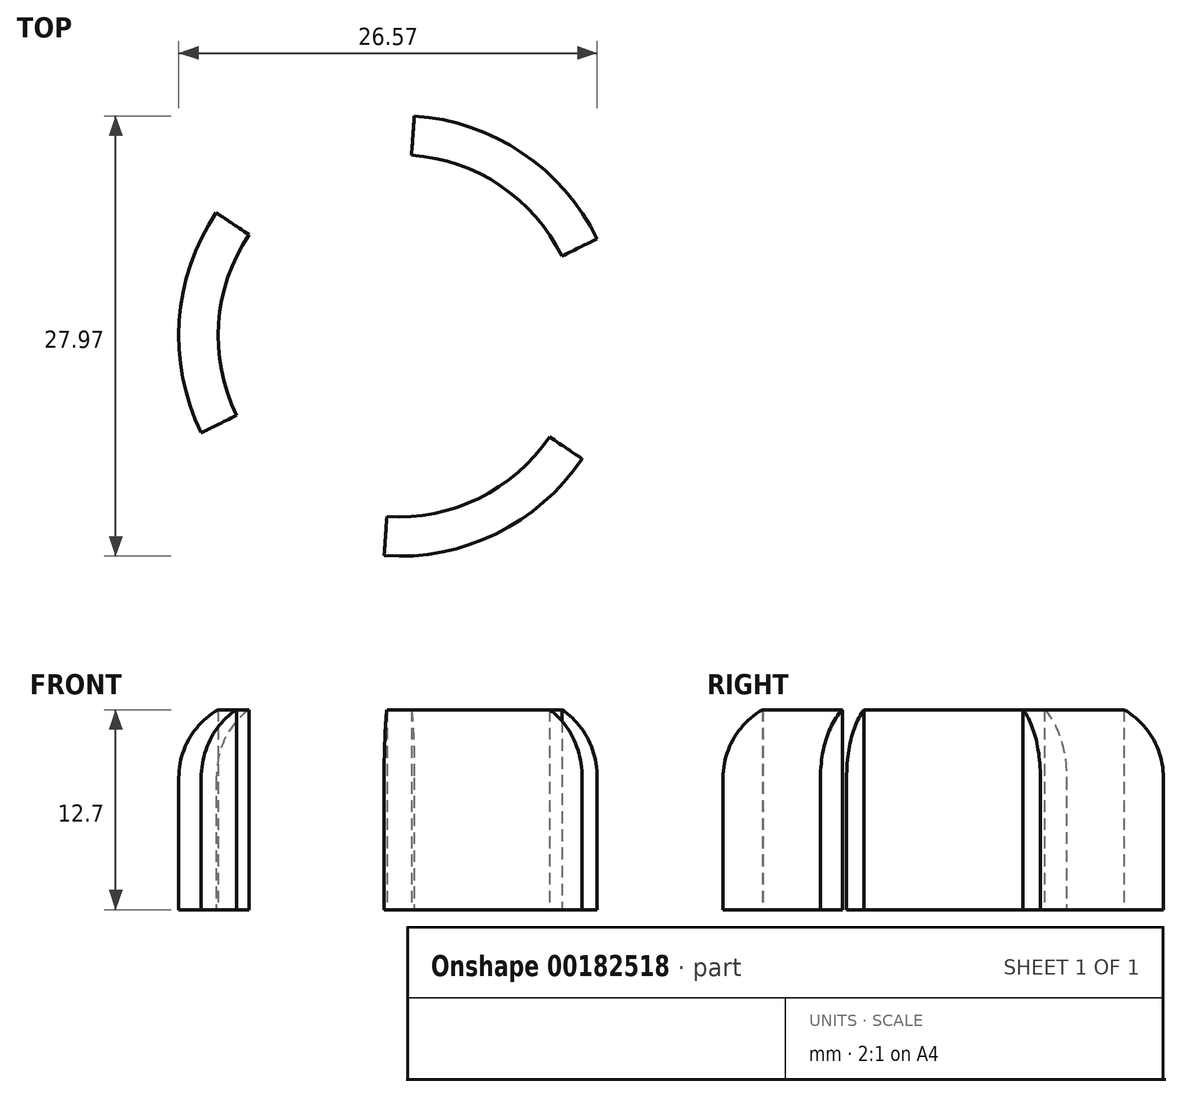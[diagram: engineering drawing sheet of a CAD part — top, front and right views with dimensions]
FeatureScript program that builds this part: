
annotation { "Feature Type Name" : "Feature", "Feature Type Description" : "" }
export const myFeature = defineFeature(function(context is Context, id is Id, definition is map)
    precondition{}
    {
        {
            var Q0;
            Q0=qCreatedBy(makeId("Top.planeOp"),FACE);
            var sketch = newSketch(context, id + "F0", { "sketchPlane" : qUnion([Q0])});
            skCircle(sketch, "E0", {"center": v(0, 0) * mm, "radius": 14 * mm});
            skLineSegment(sketch, "E1", {"start": v(0, 0) * mm, "end": v(12.57, 6.16) * mm});
            skLineSegment(sketch, "E2", {"start": v(0, 0) * mm, "end": v(11.62, -7.81) * mm});
            skLineSegment(sketch, "E3", {"start": v(0, 0) * mm, "end": v(-12.57, -6.16) * mm});
            skLineSegment(sketch, "E4", {"start": v(0, 0) * mm, "end": v(-11.62, 7.81) * mm});
            skLineSegment(sketch, "E5", {"start": v(0, 0) * mm, "end": v(0.96, 13.97) * mm});
            skLineSegment(sketch, "E6", {"start": v(0, 0) * mm, "end": v(-0.96, -13.97) * mm});
            skCircle(sketch, "E7", {"center": v(0, 0) * mm, "radius": 11.5 * mm});
            skSolve(sketch);
        }
        {
            var Q0;
            {var subQ0=sQuery(id+"F0.wireOp",EDGE,"E1");var subQ1=sQuery(id+"F0.wireOp",EDGE,"E0");var subQ2=makeQuery(id+"F0.imprint","INTERSECT",VERTEX,{"derivedFrom":[subQ1,subQ0]});Q0=makeQuery(id+"F0.imprint","IMPRINT",FACE,{"disambiguationData":[TD([[makeQuery(id+"F0.imprint","IMPRINT",EDGE,{"disambiguationData":[TD([[subQ2,-1.0]])],"derivedFrom":subQ1}),1.0]])]});}
            var Q1;
            {var subQ0=sQuery(id+"F0.wireOp",EDGE,"E2");var subQ1=sQuery(id+"F0.wireOp",EDGE,"E0");var subQ2=makeQuery(id+"F0.imprint","INTERSECT",VERTEX,{"derivedFrom":[subQ1,subQ0]});Q1=makeQuery(id+"F0.imprint","IMPRINT",FACE,{"disambiguationData":[TD([[makeQuery(id+"F0.imprint","IMPRINT",EDGE,{"disambiguationData":[TD([[subQ2,1.0]])],"derivedFrom":subQ1}),1.0]])]});}
            var Q2;
            {var subQ0=sQuery(id+"F0.wireOp",EDGE,"E3");var subQ1=sQuery(id+"F0.wireOp",EDGE,"E0");var subQ2=makeQuery(id+"F0.imprint","INTERSECT",VERTEX,{"derivedFrom":[subQ1,subQ0]});Q2=makeQuery(id+"F0.imprint","IMPRINT",FACE,{"disambiguationData":[TD([[makeQuery(id+"F0.imprint","IMPRINT",EDGE,{"disambiguationData":[TD([[subQ2,1.0]])],"derivedFrom":subQ1}),1.0]])]});}
            extrude(context, id + "F1", {"entities" : qUnion([Q0, Q1, Q2]), "depth" : 12.7 * mm});
        }
        {
            var Q0;
            {var subQ0=sQuery(id+"F0.wireOp",EDGE,"E0");Q0=makeQuery(id+"F1.opExtrude","CAP_EDGE",EDGE,{"disambiguationData":[OSD([subQ0]),TDD([makeQuery(id+"F0.imprint","IMPRINT",EDGE,{"disambiguationData":[TD([[makeQuery(id+"F0.imprint","INTERSECT",VERTEX,{"derivedFrom":[subQ0,sQuery(id+"F0.wireOp",EDGE,"E3")]}),1.0]])],"derivedFrom":subQ0})])],"isStart":false});}
            fillet(context, id + "F2", {"entities" : qUnion([Q0]), "radius" : 5 * mm, "tangentPropagation" : true, "allowEdgeOverflow" : false});
        }
        {
            var Q0;
            {var subQ0=sQuery(id+"F0.wireOp",EDGE,"E0");Q0=makeQuery(id+"F1.opExtrude","CAP_EDGE",EDGE,{"disambiguationData":[OSD([subQ0]),TDD([makeQuery(id+"F0.imprint","IMPRINT",EDGE,{"disambiguationData":[TD([[makeQuery(id+"F0.imprint","INTERSECT",VERTEX,{"derivedFrom":[subQ0,sQuery(id+"F0.wireOp",EDGE,"E1")]}),-1.0]])],"derivedFrom":subQ0})])],"isStart":false});}
            fillet(context, id + "F3", {"entities" : qUnion([Q0]), "radius" : 5 * mm, "tangentPropagation" : true, "allowEdgeOverflow" : false});
        }
        {
            var Q0;
            {var subQ0=sQuery(id+"F0.wireOp",EDGE,"E0");Q0=makeQuery(id+"F1.opExtrude","CAP_EDGE",EDGE,{"disambiguationData":[OSD([subQ0]),TDD([makeQuery(id+"F0.imprint","IMPRINT",EDGE,{"disambiguationData":[TD([[makeQuery(id+"F0.imprint","INTERSECT",VERTEX,{"derivedFrom":[subQ0,sQuery(id+"F0.wireOp",EDGE,"E2")]}),1.0]])],"derivedFrom":subQ0})])],"isStart":false});}
            fillet(context, id + "F4", {"entities" : qUnion([Q0]), "radius" : 5 * mm, "tangentPropagation" : true, "allowEdgeOverflow" : false});
        }
    });
